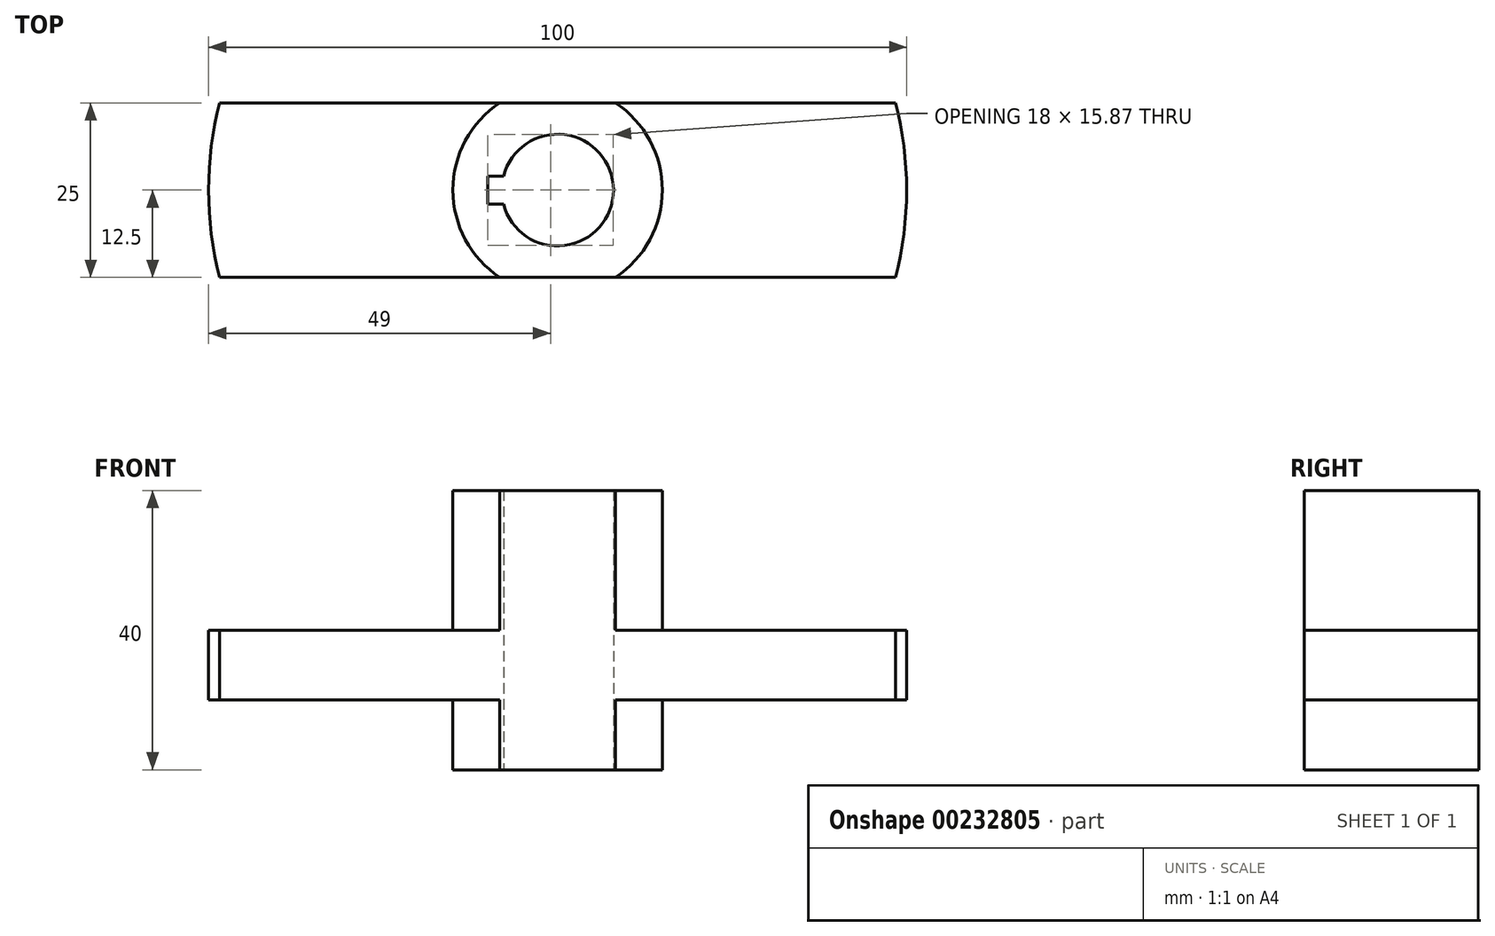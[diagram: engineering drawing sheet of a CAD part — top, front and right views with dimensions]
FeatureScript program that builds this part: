
annotation { "Feature Type Name" : "Feature", "Feature Type Description" : "" }
export const myFeature = defineFeature(function(context is Context, id is Id, definition is map)
    precondition{}
    {
        {
            var Q0;
            Q0=qCreatedBy(makeId("Top.planeOp"),FACE);
            var sketch = newSketch(context, id + "F0", { "sketchPlane" : qUnion([Q0])});
            skArc(sketch, "E0", {"start": v(-48.41, 12.5) * mm, "mid": v(-50, 0) * mm, "end": v(-48.41, -12.5) * mm});
            skArc(sketch, "E1", {"start": v(-8.3, 12.5) * mm, "mid": v(-15, 0) * mm, "end": v(-8.3, -12.5) * mm});
            skArc(sketch, "E2", {"start": v(-7.75, -2) * mm, "mid": v(8, 0) * mm, "end": v(-7.75, 2) * mm});
            skLineSegment(sketch, "E3.bottom", {"start": v(48.41, 12.5) * mm, "end": v(-48.41, 12.5) * mm});
            skLineSegment(sketch, "E3.top", {"start": v(48.41, -12.5) * mm, "end": v(-48.41, -12.5) * mm});
            skLineSegment(sketch, "E4.bottom", {"start": v(-10, 2) * mm, "end": v(-7.75, 2) * mm});
            skLineSegment(sketch, "E4.top", {"start": v(-10, -2) * mm, "end": v(-7.75, -2) * mm});
            skLineSegment(sketch, "E4.left", {"start": v(-10, 2) * mm, "end": v(-10, -2) * mm});
            skPoint(sketch, "E3.right.start.orphan", {"position": v(-62.05, 12.5) * mm});
            skPoint(sketch, "E5.orphan", {"position": v(-62.05, -12.5) * mm});
            skPoint(sketch, "E3.left.start.orphan", {"position": v(62.05, 12.5) * mm});
            skPoint(sketch, "E6.orphan", {"position": v(62.05, -12.5) * mm});
            skArc(sketch, "E7.trimOffspring", {"start": v(48.41, -12.5) * mm, "mid": v(50, 0) * mm, "end": v(48.41, 12.5) * mm});
            skArc(sketch, "E8.trimOffspring", {"start": v(8.3, -12.5) * mm, "mid": v(15, 0) * mm, "end": v(8.3, 12.5) * mm});
            skSolve(sketch);
        }
        {
            var Q0;
            {var subQ1=sQuery(id+"F0.wireOp",EDGE,"E1");Q0=makeQuery(id+"F0.imprint","IMPRINT",FACE,{"disambiguationData":[TD([[makeQuery(id+"F0.imprint","IMPRINT",EDGE,{"derivedFrom":subQ1}),1.0]])]});}
            extrude(context, id + "F1", {"entities" : qUnion([Q0]), "depth" : 30 * mm, "hasSecondDirection" : true, "secondDirectionOppositeDirection" : true, "secondDirectionDepth" : 10 * mm});
        }
        {
            var Q0;
            {var subQ0=sQuery(id+"F0.wireOp",EDGE,"E0");Q0=makeQuery(id+"F0.imprint","IMPRINT",FACE,{"disambiguationData":[TD([[makeQuery(id+"F0.imprint","IMPRINT",EDGE,{"derivedFrom":subQ0}),1.0]])]});}
            var Q1;
            {var subQ0=sQuery(id+"F0.wireOp",EDGE,"E7.trimOffspring");Q1=makeQuery(id+"F0.imprint","IMPRINT",FACE,{"disambiguationData":[TD([[makeQuery(id+"F0.imprint","IMPRINT",EDGE,{"derivedFrom":subQ0}),1.0]])]});}
            extrude(context, id + "F2", {"entities" : qUnion([Q0, Q1]), "operationType" : NewBodyOperationType.ADD, "depth" : 10 * mm});
        }
    });
